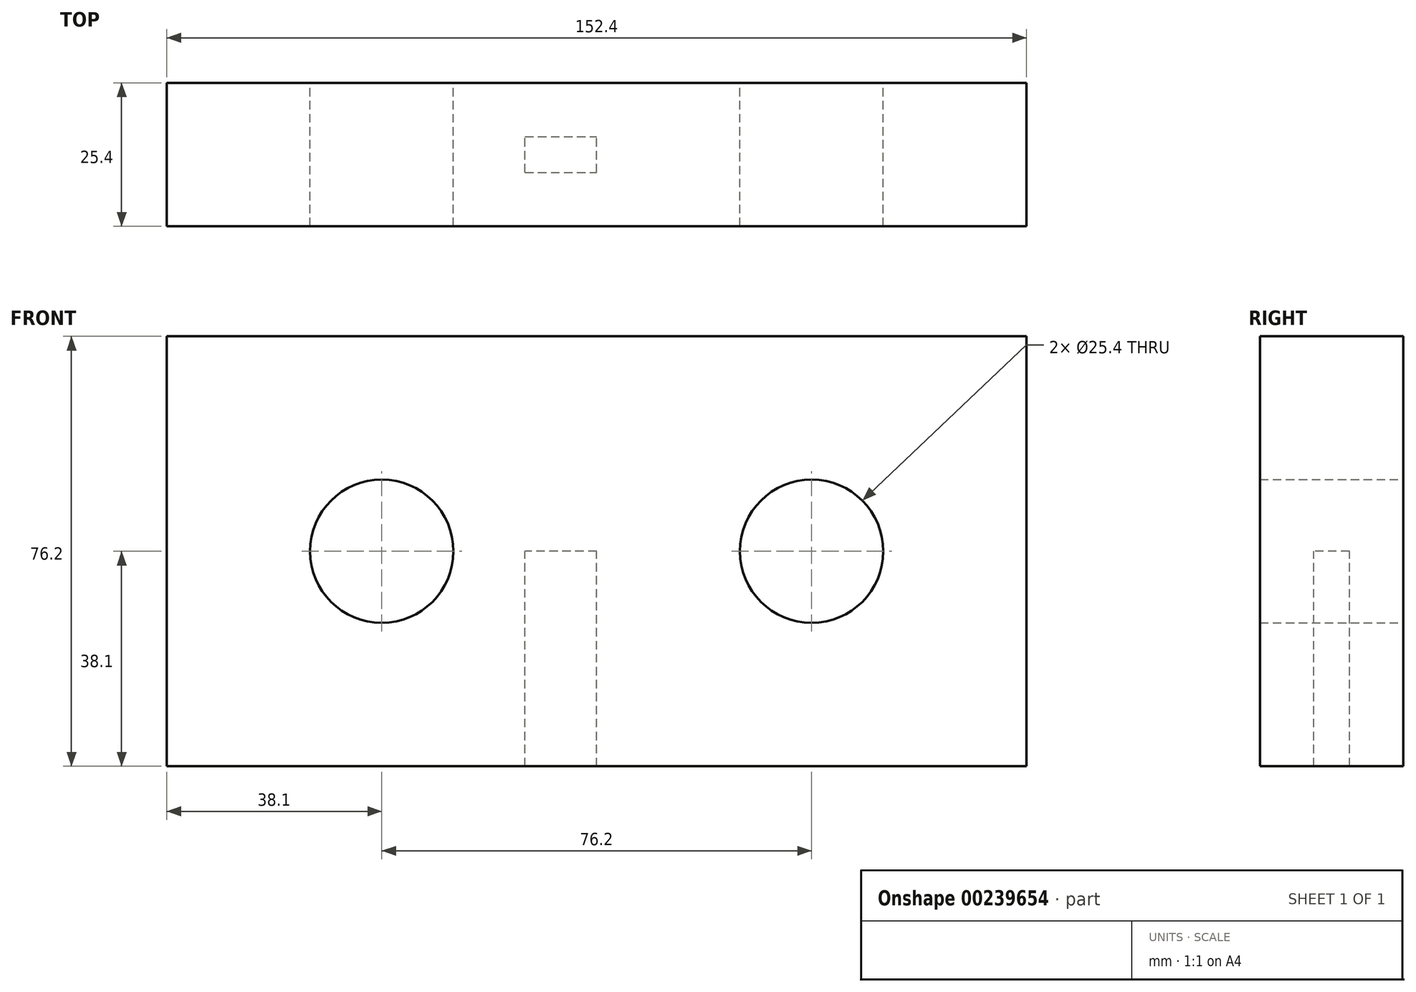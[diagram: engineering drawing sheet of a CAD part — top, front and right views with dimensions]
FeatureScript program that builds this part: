
annotation { "Feature Type Name" : "Feature", "Feature Type Description" : "" }
export const myFeature = defineFeature(function(context is Context, id is Id, definition is map)
    precondition{}
    {
        {
            var Q0;
            Q0=qCreatedBy(makeId("Front.planeOp"),FACE);
            var sketch = newSketch(context, id + "F0", { "sketchPlane" : qUnion([Q0])});
            skLineSegment(sketch, "E0.bottom", {"start": v(76.2, -38.1) * mm, "end": v(-76.2, -38.1) * mm});
            skLineSegment(sketch, "E0.top", {"start": v(76.2, 38.1) * mm, "end": v(-76.2, 38.1) * mm});
            skLineSegment(sketch, "E0.left", {"start": v(76.2, -38.1) * mm, "end": v(76.2, 38.1) * mm});
            skLineSegment(sketch, "E0.right", {"start": v(-76.2, -38.1) * mm, "end": v(-76.2, 38.1) * mm});
            skPoint(sketch, "E0.middle", {"position": v(0, 0) * mm});
            skPoint(sketch, "E1.second.point", {"position": v(-76.2, 0) * mm});
            skPoint(sketch, "E1.third.point", {"position": v(-38.49, 38.1) * mm});
            skCircle(sketch, "E2", {"center": v(-38.1, 0) * mm, "radius": 12.7 * mm});
            skCircle(sketch, "E3", {"center": v(38.1, 0) * mm, "radius": 12.7 * mm});
            skSolve(sketch);
        }
        {
            var Q0;
            Q0=qCreatedBy(makeId("Top.planeOp"),FACE);
            var sketch = newSketch(context, id + "F1", { "sketchPlane" : qUnion([Q0])});
            skLineSegment(sketch, "E4.bottom", {"start": v(0, -9.52) * mm, "end": v(-12.7, -9.52) * mm});
            skLineSegment(sketch, "E4.top", {"start": v(0, -15.87) * mm, "end": v(-12.7, -15.87) * mm});
            skLineSegment(sketch, "E4.left", {"start": v(0, -9.52) * mm, "end": v(0, -15.87) * mm});
            skLineSegment(sketch, "E4.right", {"start": v(-12.7, -9.53) * mm, "end": v(-12.7, -15.87) * mm});
            skLineSegment(sketch, "E5", {"start": v(0, 0) * mm, "end": v(-5.9, 0) * mm});
            skSolve(sketch);
        }
        {
            var Q0;
            Q0 = qSketchRegion(id + "F0", true);
            extrude(context, id + "F2", {"entities" : qUnion([Q0]), "depth" : 25.4 * mm});
        }
        {
            var Q0;
            Q0 = qSketchRegion(id + "F1", true);
            extrude(context, id + "F3", {"entities" : qUnion([Q0]), "operationType" : NewBodyOperationType.REMOVE, "oppositeDirection" : true, "depth" : 66.04 * mm});
        }
    });
